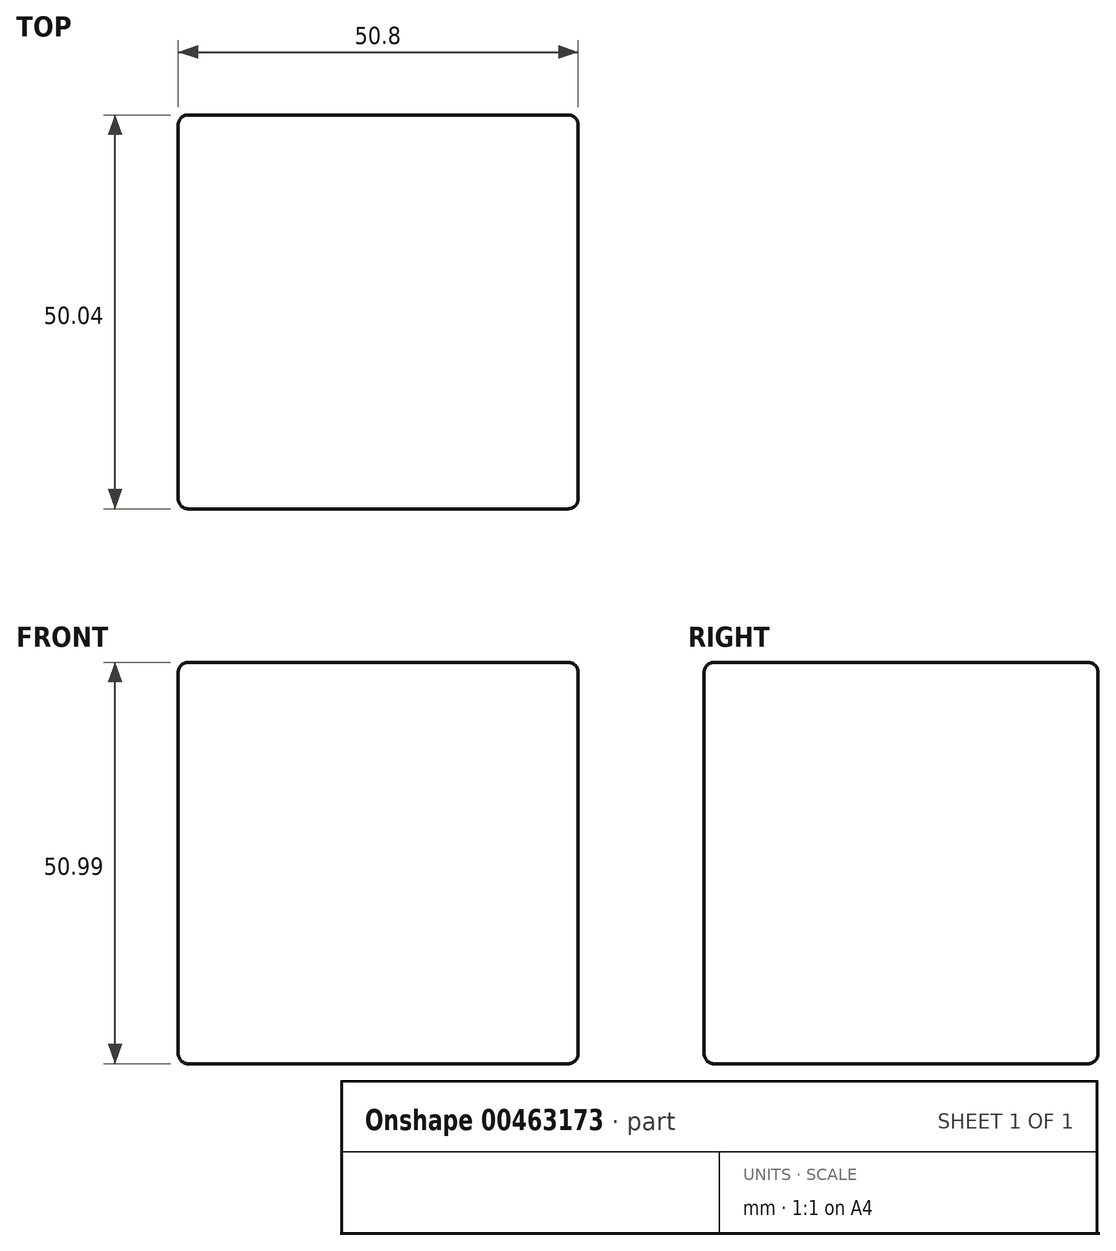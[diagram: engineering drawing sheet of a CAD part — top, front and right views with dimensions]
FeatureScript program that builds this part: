
annotation { "Feature Type Name" : "Feature", "Feature Type Description" : "" }
export const myFeature = defineFeature(function(context is Context, id is Id, definition is map)
    precondition{}
    {
        {
            var Q0;
            Q0=qCreatedBy(makeId("Front.planeOp"),FACE);
            var sketch = newSketch(context, id + "F0", { "sketchPlane" : qUnion([Q0])});
            skLineSegment(sketch, "E0.bottom", {"start": v(0, 0) * mm, "end": v(50.8, 0) * mm});
            skLineSegment(sketch, "E0.top", {"start": v(0, 50.99) * mm, "end": v(50.8, 50.99) * mm});
            skLineSegment(sketch, "E0.left", {"start": v(0, 0) * mm, "end": v(0, 50.99) * mm});
            skLineSegment(sketch, "E0.right", {"start": v(50.8, 0) * mm, "end": v(50.8, 50.99) * mm});
            skSolve(sketch);
        }
        {
            var Q0;
            Q0=makeQuery(id+"F0.imprint","IMPRINT",FACE,{"disambiguationData":[TD([[makeQuery(id+"F0.imprint","IMPRINT",EDGE,{"derivedFrom":sQuery(id+"F0.wireOp",EDGE,"E0.bottom")}),1.0]])]});
            var Q1;
            Q1=sQuery(id+"F0.wireOp",EDGE,"E0.left");
            extrude(context, id + "F1", {"entities" : qUnion([Q0]), "surfaceEntities" : qUnion([Q1]), "depth" : 50.04 * mm});
        }
        {
            var Q0;
            Q0=makeQuery(id+"F1.opExtrude","SWEPT_EDGE",EDGE,{"disambiguationData":[OSD([sQuery(id+"F0.wireOp",EDGE,"E0.top"),sQuery(id+"F0.wireOp",EDGE,"E0.left")])]});
            var Q1;
            Q1=makeQuery(id+"F1.opExtrude","SWEPT_EDGE",EDGE,{"disambiguationData":[OSD([sQuery(id+"F0.wireOp",EDGE,"E0.bottom"),sQuery(id+"F0.wireOp",EDGE,"E0.left")])]});
            var Q2;
            Q2=makeQuery(id+"F1.opExtrude","SWEPT_EDGE",EDGE,{"disambiguationData":[OSD([sQuery(id+"F0.wireOp",EDGE,"E0.top"),sQuery(id+"F0.wireOp",EDGE,"E0.right")])]});
            var Q3;
            Q3=makeQuery(id+"F1.opExtrude","CAP_EDGE",EDGE,{"disambiguationData":[OSD([sQuery(id+"F0.wireOp",EDGE,"E0.left")])],"isStart":false});
            var Q4;
            Q4=makeQuery(id+"F1.opExtrude","CAP_EDGE",EDGE,{"disambiguationData":[OSD([sQuery(id+"F0.wireOp",EDGE,"E0.top")])],"isStart":false});
            var Q5;
            Q5=makeQuery(id+"F1.opExtrude","CAP_EDGE",EDGE,{"disambiguationData":[OSD([sQuery(id+"F0.wireOp",EDGE,"E0.left")])],"isStart":true});
            var Q6;
            Q6=makeQuery(id+"F1.opExtrude","CAP_EDGE",EDGE,{"disambiguationData":[OSD([sQuery(id+"F0.wireOp",EDGE,"E0.bottom")])],"isStart":false});
            var Q7;
            Q7=makeQuery(id+"F1.opExtrude","CAP_EDGE",EDGE,{"disambiguationData":[OSD([sQuery(id+"F0.wireOp",EDGE,"E0.top")])],"isStart":true});
            var Q8;
            Q8=makeQuery(id+"F1.opExtrude","CAP_EDGE",EDGE,{"disambiguationData":[OSD([sQuery(id+"F0.wireOp",EDGE,"E0.right")])],"isStart":false});
            var Q9;
            Q9=makeQuery(id+"F1.opExtrude","SWEPT_EDGE",EDGE,{"disambiguationData":[OSD([sQuery(id+"F0.wireOp",EDGE,"E0.bottom"),sQuery(id+"F0.wireOp",EDGE,"E0.right")])]});
            var Q10;
            Q10=makeQuery(id+"F1.opExtrude","CAP_EDGE",EDGE,{"disambiguationData":[OSD([sQuery(id+"F0.wireOp",EDGE,"E0.right")])],"isStart":true});
            var Q11;
            Q11=makeQuery(id+"F1.opExtrude","CAP_EDGE",EDGE,{"disambiguationData":[OSD([sQuery(id+"F0.wireOp",EDGE,"E0.bottom")])],"isStart":true});
            fillet(context, id + "F2", {"entities" : qUnion([Q0, Q1, Q2, Q3, Q4, Q5, Q6, Q7, Q8, Q9, Q10, Q11]), "radius" : 1.27 * mm, "tangentPropagation" : true, "allowEdgeOverflow" : false});
        }
    });
